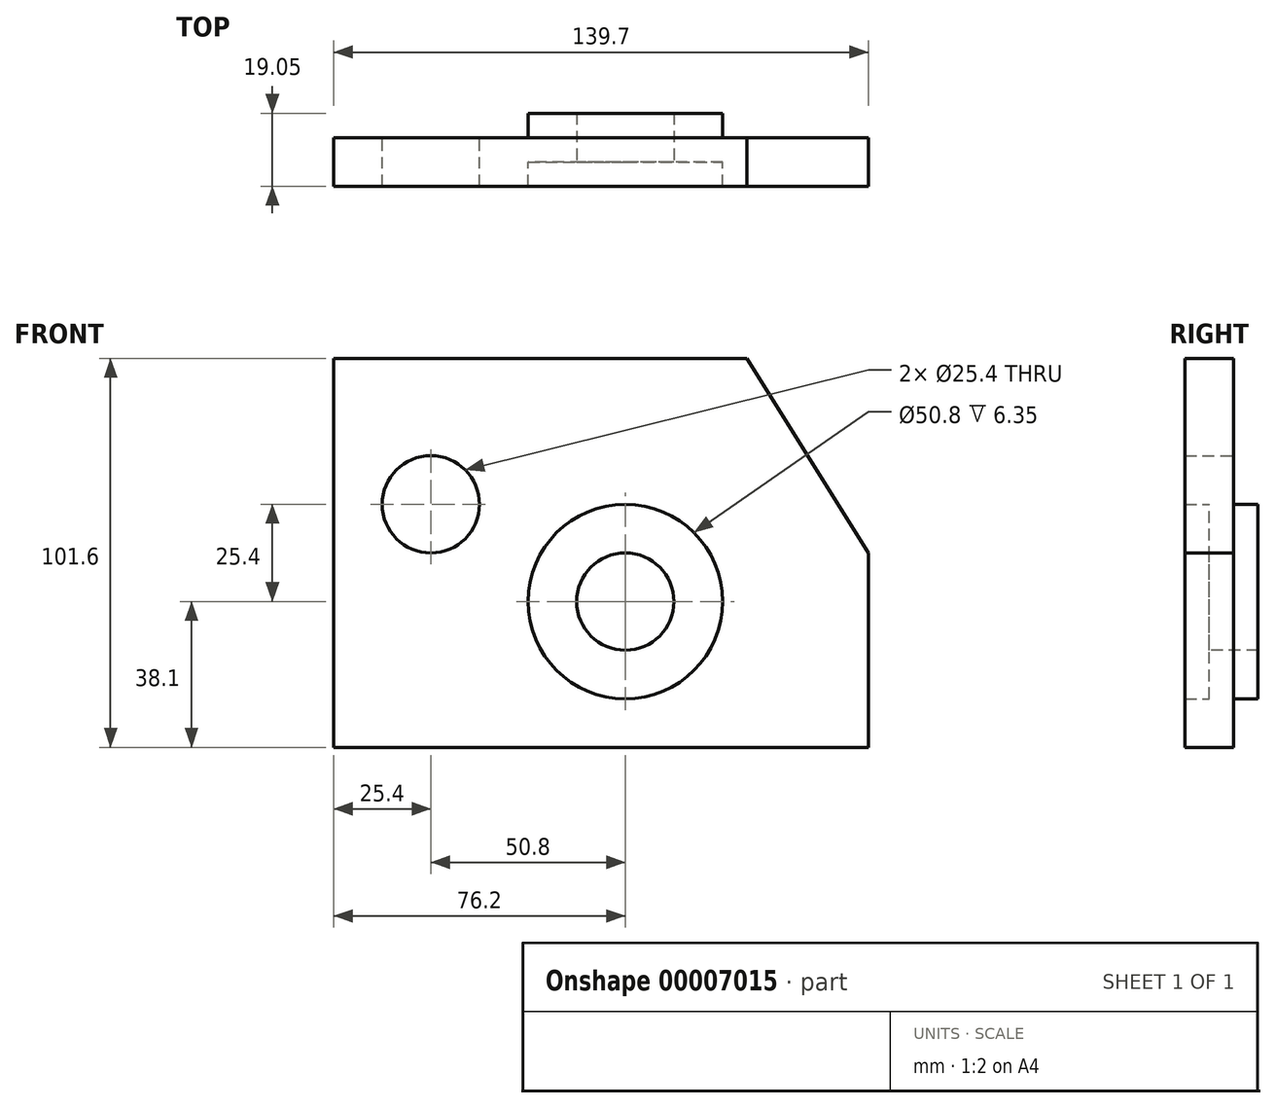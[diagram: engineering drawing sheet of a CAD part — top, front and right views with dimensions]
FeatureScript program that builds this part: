
annotation { "Feature Type Name" : "Feature", "Feature Type Description" : "" }
export const myFeature = defineFeature(function(context is Context, id is Id, definition is map)
    precondition{}
    {
        {
            var Q0;
            Q0=qCreatedBy(makeId("Front.planeOp"),FACE);
            var sketch = newSketch(context, id + "F0", { "sketchPlane" : qUnion([Q0])});
            skLineSegment(sketch, "E0", {"start": v(-76.2, -38.1) * mm, "end": v(63.5, -38.1) * mm});
            skLineSegment(sketch, "E1", {"start": v(-76.2, -38.1) * mm, "end": v(-76.2, 63.5) * mm});
            skLineSegment(sketch, "E2", {"start": v(-76.2, 63.5) * mm, "end": v(31.75, 63.5) * mm});
            skLineSegment(sketch, "E3", {"start": v(31.75, 63.5) * mm, "end": v(63.5, 12.7) * mm});
            skLineSegment(sketch, "E4", {"start": v(63.5, 12.7) * mm, "end": v(63.5, -38.1) * mm});
            skCircle(sketch, "E5", {"center": v(0, 0) * mm, "radius": 12.7 * mm});
            skCircle(sketch, "E6", {"center": v(0, 0) * mm, "radius": 25.4 * mm});
            skCircle(sketch, "E7", {"center": v(-50.8, 25.4) * mm, "radius": 12.7 * mm});
            skSolve(sketch);
        }
        {
            var Q0;
            Q0 = qSketchRegion(id + "F0", true);
            extrude(context, id + "F1", {"entities" : qUnion([Q0]), "endBound" : BoundingType.SYMMETRIC, "depth" : 12.7 * mm});
        }
        {
            var Q0;
            Q0=makeQuery(id+"F0.imprint","IMPRINT",FACE,{"disambiguationData":[TD([[makeQuery(id+"F0.imprint","IMPRINT",EDGE,{"derivedFrom":sQuery(id+"F0.wireOp",EDGE,"E5")}),-1.0]])]});
            extrude(context, id + "F2", {"entities" : qUnion([Q0]), "operationType" : NewBodyOperationType.ADD, "oppositeDirection" : true, "depth" : 12.7 * mm});
        }
    });
